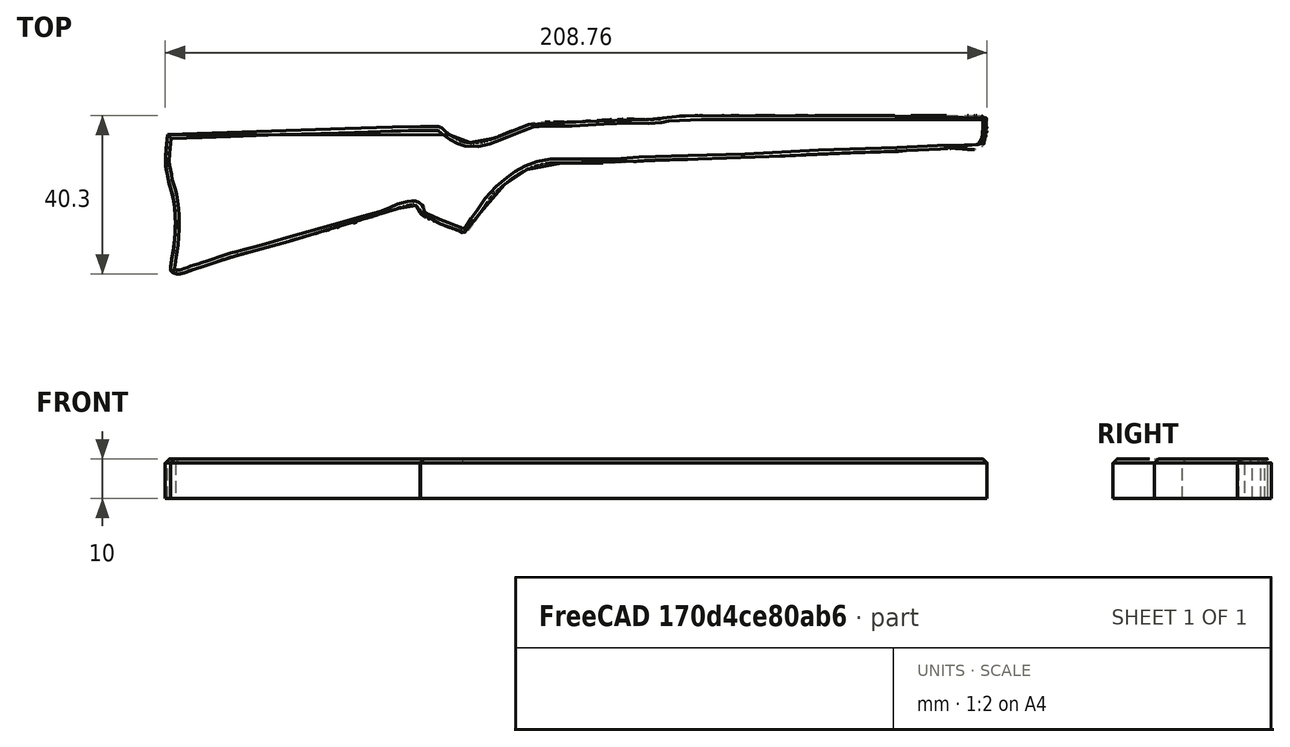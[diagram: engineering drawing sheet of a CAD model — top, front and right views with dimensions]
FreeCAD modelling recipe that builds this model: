
FCSTD DOCUMENT  (FreeCAD 1.0R39319 (Git))
Label: rifel_outline2
License: All rights reserved
LicenseURL: https://en.wikipedia.org/wiki/All_rights_reserved
objects: Image::ImagePlane×1, Sketcher::SketchObject×1, PartDesign::Pad×1, PartDesign::Chamfer×1, PartDesign::Body×1
note: 9 computed .brp shape members not serialized (recipe doc carries the construction recipe); baked Part::Feature solids carry a one-line shape summary decoded from their .brp

FEATURE [Image::ImagePlane] gun
  XSize = 292.416
  YSize = 74.0741
FEATURE [Sketcher::SketchObject] Sketch
  ArcFitTolerance = 1e-06
  AttachmentSupport = -> [XY_Plane]
  FullyConstrained = false
  MakeInternals = false
  MapMode = 5
  sketch-geometry (176):
    g0-g68: Circle [constr] x69 (B-spline internal-alignment scaffolding for g69; pole/knot coordinates omitted)
    g69: BSplineCurve PolesCount=69 KnotsCount=67 Degree=3 IsPeriodic=0
    g70-g136: GeomPoint [constr] x67 (B-spline internal-alignment scaffolding for g69; pole/knot coordinates omitted)
    g137-g156: Circle [constr] x20 (B-spline internal-alignment scaffolding for g157; pole/knot coordinates omitted)
    g157: BSplineCurve PolesCount=20 KnotsCount=18 Degree=3 IsPeriodic=0
    g158-g175: GeomPoint [constr] x18 (B-spline internal-alignment scaffolding for g157; pole/knot coordinates omitted)
  constraints (27):
    c: Weight(g0) = 1
    c: Equal(g0, g1-g68) x68
    c: InternalAlignment(g0-g68 -> g69) x69
    c: InternalAlignment(g70-g136 -> g69) x67
    c: PointOnObject(g3,g2)
    c: PointOnObject(g6,g5)
    c: PointOnObject(g10,g9)
    c: PointOnObject(g21,g20)
    c: PointOnObject(g27,g26)
    c: PointOnObject(g39,g-1)
    c: PointOnObject(g40,g-1)
    c: PointOnObject(g41,g-1)
    c: PointOnObject(g42,g-1)
    c: PointOnObject(g54,g53)
    c: PointOnObject(g58,g57)
    c: PointOnObject(g59,g57)
    c: PointOnObject(g60,g58)
    c: PointOnObject(g61,g60)
    c: PointOnObject(g62,g61)
    c: Weight(g137) = 1
    c: Equal(g137, g138-g156) x19
    c: InternalAlignment(g137-g156 -> g157) x20
    c: InternalAlignment(g158-g175 -> g157) x18
    c: Coincident(g137,g69)
    c: PointOnObject(g139,g-1)
    c: PointOnObject(g149,g147)
    c: Coincident(g156,g69)
FEATURE [PartDesign::Pad] Pad
  Direction = (0,0,1)
  Length = 10
  Length2 = 10
  Profile = -> Sketch
  ReferenceAxis = -> Sketch [N_Axis]
  Refine = true
  Suppressed = false
  Type = 0
FEATURE [PartDesign::Chamfer] Chamfer
  Angle = 45
  Base = -> Pad [Face4]
  BaseFeature = -> Pad
  ChamferType = 0
  FlipDirection = false
  Refine = true
  Size = 1
  Size2 = 1
  SupportTransform = false
  Suppressed = false
  UseAllEdges = false
FEATURE [PartDesign::Body] Body
  AllowCompound = false
  Group = -> [Sketch,Pad,Chamfer]
  Origin = -> Origin
  Tip = -> Chamfer
